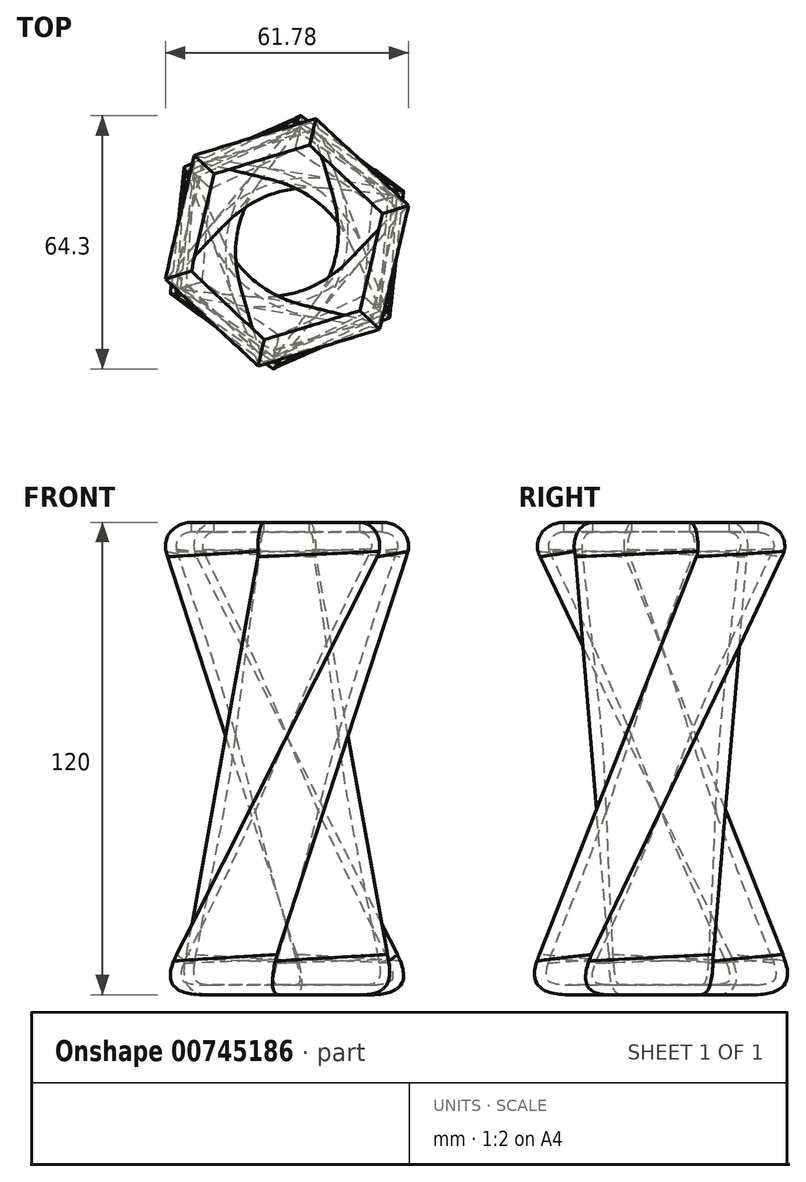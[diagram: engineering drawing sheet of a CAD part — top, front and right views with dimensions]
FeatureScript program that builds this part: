
annotation { "Feature Type Name" : "Feature", "Feature Type Description" : "" }
export const myFeature = defineFeature(function(context is Context, id is Id, definition is map)
    precondition{}
    {
        {
            var Q0;
            Q0=qCreatedBy(makeId("Top.planeOp"),FACE);
            var sketch = newSketch(context, id + "F0", { "sketchPlane" : qUnion([Q0])});
            skCircle(sketch, "E0.cCircle", {"center": v(0, 0) * mm, "radius": 30.67 * mm, "construction": true});
            skLineSegment(sketch, "E0.0", {"start": v(-33.17, -12.42) * mm, "end": v(-27.34, 22.5) * mm});
            skLineSegment(sketch, "E0.1", {"start": v(-27.34, 22.5) * mm, "end": v(5.82, 34.93) * mm});
            skLineSegment(sketch, "E0.2", {"start": v(5.82, 34.93) * mm, "end": v(33.17, 12.42) * mm});
            skLineSegment(sketch, "E0.3", {"start": v(33.17, 12.42) * mm, "end": v(27.34, -22.5) * mm});
            skLineSegment(sketch, "E0.4", {"start": v(27.34, -22.5) * mm, "end": v(-5.82, -34.93) * mm});
            skLineSegment(sketch, "E0.5", {"start": v(-5.82, -34.93) * mm, "end": v(-33.17, -12.42) * mm});
            skPoint(sketch, "E0.0.midPoint", {"position": v(-30.25, 5.04) * mm});
            skSolve(sketch);
        }
        {
            var Q0;
            Q0=qCreatedBy(makeId("Top.planeOp"),FACE);
            cPlane(context, id + "F1", {"entities" : qUnion([Q0]), "cplaneType" : CPlaneType.OFFSET, "offset" : 120 * mm, "width" : 150 * mm, "height" : 150 * mm});
        }
        {
            var Q0;
            Q0=qCreatedBy(id+"F1.planeOp",FACE);
            var sketch = newSketch(context, id + "F2", { "sketchPlane" : qUnion([Q0])});
            skLineSegment(sketch, "E1.0", {"start": v(-5.82, -34.93) * mm, "end": v(-33.17, -12.42) * mm});
            skLineSegment(sketch, "E1.1", {"start": v(-33.17, -12.42) * mm, "end": v(-27.34, 22.5) * mm});
            skLineSegment(sketch, "E1.2", {"start": v(-27.34, 22.5) * mm, "end": v(5.82, 34.93) * mm});
            skLineSegment(sketch, "E1.3", {"start": v(5.82, 34.93) * mm, "end": v(33.17, 12.42) * mm});
            skLineSegment(sketch, "E1.4", {"start": v(33.17, 12.42) * mm, "end": v(27.34, -22.5) * mm});
            skLineSegment(sketch, "E1.5", {"start": v(27.34, -22.5) * mm, "end": v(-5.82, -34.93) * mm});
            skSolve(sketch);
        }
        {
            var Q0;
            Q0=makeQuery(id+"F0.imprint","IMPRINT",FACE,{"disambiguationData":[TD([[makeQuery(id+"F0.imprint","IMPRINT",EDGE,{"derivedFrom":sQuery(id+"F0.wireOp",EDGE,"E0.0")}),-1.0]])]});
            var Q1;
            Q1=makeQuery(id+"F2.imprint","IMPRINT",FACE,{"disambiguationData":[TD([[makeQuery(id+"F2.imprint","IMPRINT",EDGE,{"derivedFrom":sQuery(id+"F2.wireOp",EDGE,"E1.0")}),-1.0]])]});
            var Q2;
            Q2=sQuery(id+"F2.wireOp",VERTEX,"E1.0.start");
            var Q3;
            Q3=sQuery(id+"F0.wireOp",VERTEX,"E0.1.start");
            loft(context, id + "F3", {"sheetProfilesArray" : [{ "sheetProfileEntities" : qUnion([Q0]) }, { "sheetProfileEntities" : qUnion([Q1]) }], "matchConnections" : true, "connections" : [{ "connectionEntities" : qUnion([Q2, Q3]), "connectionEdgeQueries" : qUnion([]), "connectionEdgeParameters" : [] }]});
        }
        {
            var Q0;
            Q0=makeQuery(id+"F3.opLoft","MID_CAP_EDGE",EDGE,{"disambiguationData":[OSD([sQuery(id+"F0.wireOp",EDGE,"E0.0"),sQuery(id+"F0.wireOp",EDGE,"E0.4"),sQuery(id+"F0.wireOp",EDGE,"E0.5")])],"capPos":0.0});
            var Q1;
            Q1=makeQuery(id+"F3.opLoft","MID_CAP_EDGE",EDGE,{"disambiguationData":[OSD([sQuery(id+"F0.wireOp",EDGE,"E0.0"),sQuery(id+"F0.wireOp",EDGE,"E0.1"),sQuery(id+"F0.wireOp",EDGE,"E0.5")])],"capPos":0.0});
            var Q2;
            Q2=makeQuery(id+"F3.opLoft","CAP_FACE",FACE,{"disambiguationData":[OSD([makeQuery(id+"F0.imprint","IMPRINT",FACE,{"disambiguationData":[TD([[makeQuery(id+"F0.imprint","IMPRINT",EDGE,{"derivedFrom":sQuery(id+"F0.wireOp",EDGE,"E0.0")}),-1.0]])]})])],"isStart":true});
            fillet(context, id + "F4", {"entities" : qUnion([Q0, Q1, Q2]), "radius" : 7 * mm, "tangentPropagation" : true, "rho" : 0.5, "crossSection" : FilletCrossSection.CONIC, "allowEdgeOverflow" : false});
        }
        {
            var Q0;
            Q0=makeQuery(id+"F3.opLoft","CAP_FACE",FACE,{"disambiguationData":[OSD([makeQuery(id+"F2.imprint","IMPRINT",FACE,{"disambiguationData":[TD([[makeQuery(id+"F2.imprint","IMPRINT",EDGE,{"derivedFrom":sQuery(id+"F2.wireOp",EDGE,"E1.0")}),-1.0]])]})])],"isStart":true});
            fillet(context, id + "F5", {"entities" : qUnion([Q0]), "radius" : 6 * mm, "tangentPropagation" : true, "allowEdgeOverflow" : false});
        }
        {
            var Q0;
            Q0=makeQuery(id+"F3.opLoft","CAP_FACE",FACE,{"disambiguationData":[OSD([makeQuery(id+"F2.imprint","IMPRINT",FACE,{"disambiguationData":[TD([[makeQuery(id+"F2.imprint","IMPRINT",EDGE,{"derivedFrom":sQuery(id+"F2.wireOp",EDGE,"E1.0")}),-1.0]])]})])],"isStart":true});
            shell(context, id + "F6", {"entities" : qUnion([Q0]), "thickness" : 2.5 * mm});
        }
    });
